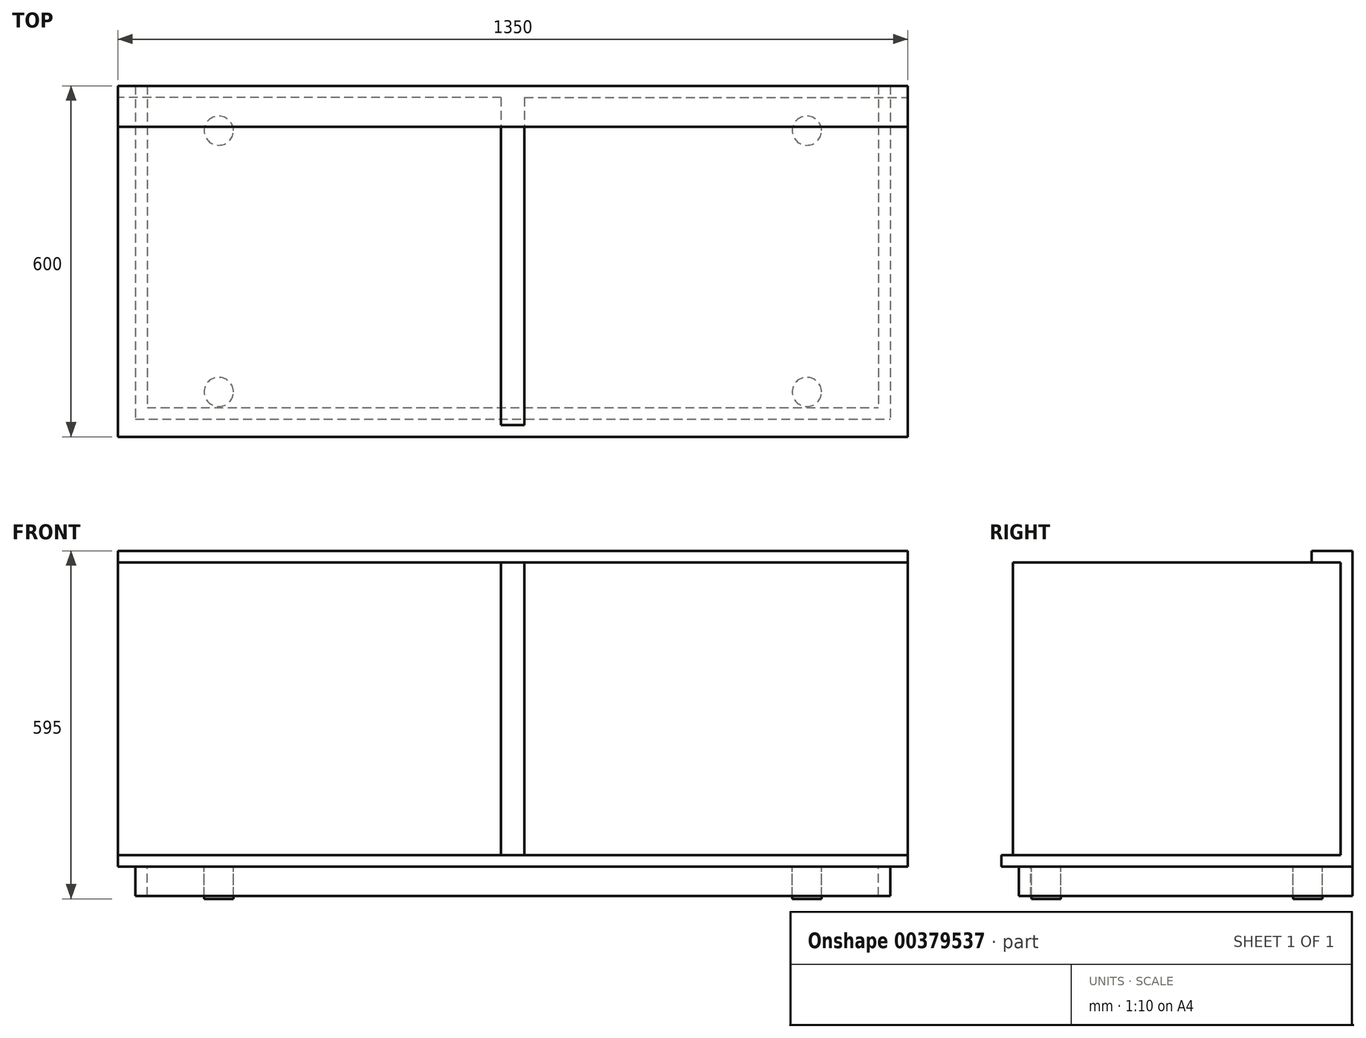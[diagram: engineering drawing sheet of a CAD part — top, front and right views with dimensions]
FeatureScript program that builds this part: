
annotation { "Feature Type Name" : "Feature", "Feature Type Description" : "" }
export const myFeature = defineFeature(function(context is Context, id is Id, definition is map)
    precondition{}
    {
        {
            var Q0;
            Q0=qCreatedBy(makeId("Top.planeOp"),FACE);
            var sketch = newSketch(context, id + "F0", { "sketchPlane" : qUnion([Q0])});
            skLineSegment(sketch, "E0.bottom", {"start": v(-655, 280) * mm, "end": v(655, 280) * mm});
            skPoint(sketch, "E0.middle", {"position": v(0, 0) * mm});
            skLineSegment(sketch, "E1.bottom", {"start": v(-675, 300) * mm, "end": v(675, 300) * mm});
            skLineSegment(sketch, "E2.bottom", {"start": v(-20, 280) * mm, "end": v(20, 280) * mm});
            skLineSegment(sketch, "E2.top", {"start": v(-20, -280) * mm, "end": v(20, -280) * mm});
            skLineSegment(sketch, "E2.left", {"start": v(-20, 280) * mm, "end": v(-20, -280) * mm});
            skLineSegment(sketch, "E2.right", {"start": v(20, 280) * mm, "end": v(20, -280) * mm});
            skLineSegment(sketch, "E3", {"start": v(0, 280) * mm, "end": v(0, -280) * mm});
            skLineSegment(sketch, "E4", {"start": v(-655, 280) * mm, "end": v(-675, 280) * mm});
            skLineSegment(sketch, "E5", {"start": v(-675, 280) * mm, "end": v(-675, 300) * mm});
            skLineSegment(sketch, "E6", {"start": v(675, 300) * mm, "end": v(675, 280) * mm});
            skLineSegment(sketch, "E7", {"start": v(675, 280) * mm, "end": v(655, 280) * mm});
            skSolve(sketch);
        }
        {
            var Q0;
            Q0=makeQuery(id+"F0.imprint","IMPRINT",FACE,{"disambiguationData":[TD([[makeQuery(id+"F0.imprint","IMPRINT",EDGE,{"derivedFrom":sQuery(id+"F0.wireOp",EDGE,"E0.bottom")}),1.0]])]});
            var Q1;
            {var subQ0=sQuery(id+"F0.wireOp",EDGE,"E2.right");Q1=makeQuery(id+"F0.imprint","IMPRINT",FACE,{"disambiguationData":[TD([[makeQuery(id+"F0.imprint","IMPRINT",EDGE,{"derivedFrom":subQ0}),-1.0]])]});}
            var Q2;
            {var subQ0=sQuery(id+"F0.wireOp",EDGE,"E2.left");Q2=makeQuery(id+"F0.imprint","IMPRINT",FACE,{"disambiguationData":[TD([[makeQuery(id+"F0.imprint","IMPRINT",EDGE,{"derivedFrom":subQ0}),1.0]])]});}
            extrude(context, id + "F1", {"entities" : qUnion([Q0, Q1, Q2]), "depth" : 500 * mm});
        }
        {
            var Q0;
            Q0=makeQuery(id+"F1.opExtrude","CAP_FACE",FACE,{"disambiguationData":[OSD([sQuery(id+"F0.wireOp",EDGE,"E0.bottom"),sQuery(id+"F0.wireOp",EDGE,"E0.top"),sQuery(id+"F0.wireOp",EDGE,"E0.left"),sQuery(id+"F0.wireOp",EDGE,"E0.right"),sQuery(id+"F0.wireOp",EDGE,"E1.bottom"),sQuery(id+"F0.wireOp",EDGE,"E1.top"),sQuery(id+"F0.wireOp",EDGE,"E1.left"),sQuery(id+"F0.wireOp",EDGE,"E1.right")])],"isStart":false});
            var sketch = newSketch(context, id + "F2", { "sketchPlane" : qUnion([Q0])});
            skLineSegment(sketch, "E8.bottom", {"start": v(-675, 300) * mm, "end": v(675, 300) * mm});
            skLineSegment(sketch, "E8.top", {"start": v(-675, 230) * mm, "end": v(675, 230) * mm});
            skLineSegment(sketch, "E8.left", {"start": v(-675, 300) * mm, "end": v(-675, 230) * mm});
            skLineSegment(sketch, "E9", {"start": v(675, 300) * mm, "end": v(675, 230) * mm});
            skSolve(sketch);
        }
        {
            var Q0;
            Q0=qSketchRegion(id+"F2",true);
            extrude(context, id + "F3", {"entities" : qUnion([Q0]), "operationType" : NewBodyOperationType.ADD, "depth" : 20 * mm});
        }
        {
            var Q0;
            Q0=makeQuery(id+"F1.opExtrude","CAP_FACE",FACE,{"disambiguationData":[OSD([sQuery(id+"F0.wireOp",EDGE,"E0.bottom"),sQuery(id+"F0.wireOp",EDGE,"E0.top"),sQuery(id+"F0.wireOp",EDGE,"E0.left"),sQuery(id+"F0.wireOp",EDGE,"E0.right"),sQuery(id+"F0.wireOp",EDGE,"E1.bottom"),sQuery(id+"F0.wireOp",EDGE,"E1.top"),sQuery(id+"F0.wireOp",EDGE,"E1.left"),sQuery(id+"F0.wireOp",EDGE,"E1.right")])],"isStart":true});
            var sketch = newSketch(context, id + "F4", { "sketchPlane" : qUnion([Q0])});
            skLineSegment(sketch, "E10.bottom", {"start": v(-675, 300) * mm, "end": v(675, 300) * mm});
            skLineSegment(sketch, "E10.top", {"start": v(-675, -300) * mm, "end": v(675, -300) * mm});
            skLineSegment(sketch, "E10.left", {"start": v(-675, 300) * mm, "end": v(-675, -300) * mm});
            skLineSegment(sketch, "E10.right", {"start": v(675, 300) * mm, "end": v(675, -300) * mm});
            skSolve(sketch);
        }
        {
            var Q0;
            Q0=qSketchRegion(id+"F4",true);
            extrude(context, id + "F5", {"entities" : qUnion([Q0]), "operationType" : NewBodyOperationType.ADD, "depth" : 20 * mm});
        }
        {
            var Q0;
            Q0=makeQuery(id+"F5.opExtrude","CAP_FACE",FACE,{"disambiguationData":[OSD([sQuery(id+"F4.wireOp",EDGE,"E10.bottom"),sQuery(id+"F4.wireOp",EDGE,"E10.top"),sQuery(id+"F4.wireOp",EDGE,"E10.left"),sQuery(id+"F4.wireOp",EDGE,"E10.right")])],"isStart":false});
            var sketch = newSketch(context, id + "F6", { "sketchPlane" : qUnion([Q0])});
            skLineSegment(sketch, "E11", {"start": v(-675, 300) * mm, "end": v(675, -300) * mm, "construction": true});
            skLineSegment(sketch, "E12", {"start": v(675, 300) * mm, "end": v(-675, -300) * mm, "construction": true});
            skLineSegment(sketch, "E13", {"start": v(0, 300) * mm, "end": v(-675, 0) * mm, "construction": true});
            skLineSegment(sketch, "E14", {"start": v(-675, 0) * mm, "end": v(675, 0) * mm, "construction": true});
            skLineSegment(sketch, "E15", {"start": v(675, 0) * mm, "end": v(0, 300) * mm, "construction": true});
            skLineSegment(sketch, "E16", {"start": v(-675, 0) * mm, "end": v(0, -300) * mm, "construction": true});
            skLineSegment(sketch, "E17", {"start": v(0, -300) * mm, "end": v(675, 0) * mm, "construction": true});
            skLineSegment(sketch, "E18", {"start": v(675, -150) * mm, "end": v(-675, -150) * mm, "construction": true});
            skPoint(sketch, "E18.startSnap0", {"position": v(337.5, -150) * mm});
            skLineSegment(sketch, "E19", {"start": v(-675, 150) * mm, "end": v(675, 150) * mm, "construction": true});
            skPoint(sketch, "E19.startSnap0", {"position": v(-337.5, 150) * mm});
            skCircle(sketch, "E20", {"center": v(0, 0) * mm, "radius": 550 * mm, "construction": true});
            skCircle(sketch, "E21", {"center": v(-502.6, 223.38) * mm, "radius": 25 * mm});
            skCircle(sketch, "E22", {"center": v(-502.6, -223.38) * mm, "radius": 25 * mm});
            skCircle(sketch, "E23", {"center": v(502.6, 223.38) * mm, "radius": 25 * mm});
            skCircle(sketch, "E24", {"center": v(502.6, -223.38) * mm, "radius": 25 * mm});
            skSolve(sketch);
        }
        {
            var Q0;
            Q0=makeQuery(id+"F6.imprint","IMPRINT",FACE,{"disambiguationData":[TD([[makeQuery(id+"F6.imprint","IMPRINT",EDGE,{"derivedFrom":sQuery(id+"F6.wireOp",EDGE,"E21")}),1.0]])]});
            var Q1;
            Q1=makeQuery(id+"F6.imprint","IMPRINT",FACE,{"disambiguationData":[TD([[makeQuery(id+"F6.imprint","IMPRINT",EDGE,{"derivedFrom":sQuery(id+"F6.wireOp",EDGE,"E22")}),1.0]])]});
            var Q2;
            Q2=makeQuery(id+"F6.imprint","IMPRINT",FACE,{"disambiguationData":[TD([[makeQuery(id+"F6.imprint","IMPRINT",EDGE,{"derivedFrom":sQuery(id+"F6.wireOp",EDGE,"E24")}),1.0]])]});
            var Q3;
            Q3=makeQuery(id+"F6.imprint","IMPRINT",FACE,{"disambiguationData":[TD([[makeQuery(id+"F6.imprint","IMPRINT",EDGE,{"derivedFrom":sQuery(id+"F6.wireOp",EDGE,"E23")}),1.0]])]});
            extrude(context, id + "F7", {"entities" : qUnion([Q0, Q1, Q2, Q3]), "operationType" : NewBodyOperationType.ADD, "depth" : 55 * mm});
        }
        {
            var Q0;
            Q0=makeQuery(id+"F5.opExtrude","CAP_FACE",FACE,{"disambiguationData":[OSD([sQuery(id+"F4.wireOp",EDGE,"E10.bottom"),sQuery(id+"F4.wireOp",EDGE,"E10.top"),sQuery(id+"F4.wireOp",EDGE,"E10.left"),sQuery(id+"F4.wireOp",EDGE,"E10.right")])],"isStart":false});
            var sketch = newSketch(context, id + "F8", { "sketchPlane" : qUnion([Q0])});
            skLineSegment(sketch, "E25.top", {"start": v(-645, 270) * mm, "end": v(645, 270) * mm});
            skLineSegment(sketch, "E25.left", {"start": v(-645, -270) * mm, "end": v(-645, 270) * mm});
            skLineSegment(sketch, "E25.right", {"start": v(645, -270) * mm, "end": v(645, 270) * mm});
            skPoint(sketch, "E25.middle", {"position": v(0, 0) * mm});
            skLineSegment(sketch, "E26.top", {"start": v(-625, 250) * mm, "end": v(625, 250) * mm});
            skLineSegment(sketch, "E26.left", {"start": v(-625, -250) * mm, "end": v(-625, 250) * mm});
            skLineSegment(sketch, "E26.right", {"start": v(625, -250) * mm, "end": v(625, 250) * mm});
            skLineSegment(sketch, "E27", {"start": v(-645, -270) * mm, "end": v(-645, -300) * mm});
            skLineSegment(sketch, "E28", {"start": v(-625, -300) * mm, "end": v(-625, -250) * mm});
            skLineSegment(sketch, "E29", {"start": v(625, -250) * mm, "end": v(625, -300) * mm});
            skLineSegment(sketch, "E30", {"start": v(645, -300) * mm, "end": v(645, -270) * mm});
            skLineSegment(sketch, "E31", {"start": v(-645, -300) * mm, "end": v(-625, -300) * mm});
            skLineSegment(sketch, "E32", {"start": v(625, -300) * mm, "end": v(645, -300) * mm});
            skSolve(sketch);
        }
        {
            var Q0;
            Q0=makeQuery(id+"F8.imprint","IMPRINT",FACE,{"disambiguationData":[TD([[makeQuery(id+"F8.imprint","IMPRINT",EDGE,{"derivedFrom":sQuery(id+"F8.wireOp",EDGE,"E25.top")}),-1.0]])]});
            extrude(context, id + "F9", {"entities" : qUnion([Q0]), "operationType" : NewBodyOperationType.ADD, "depth" : 50 * mm});
        }
    });
